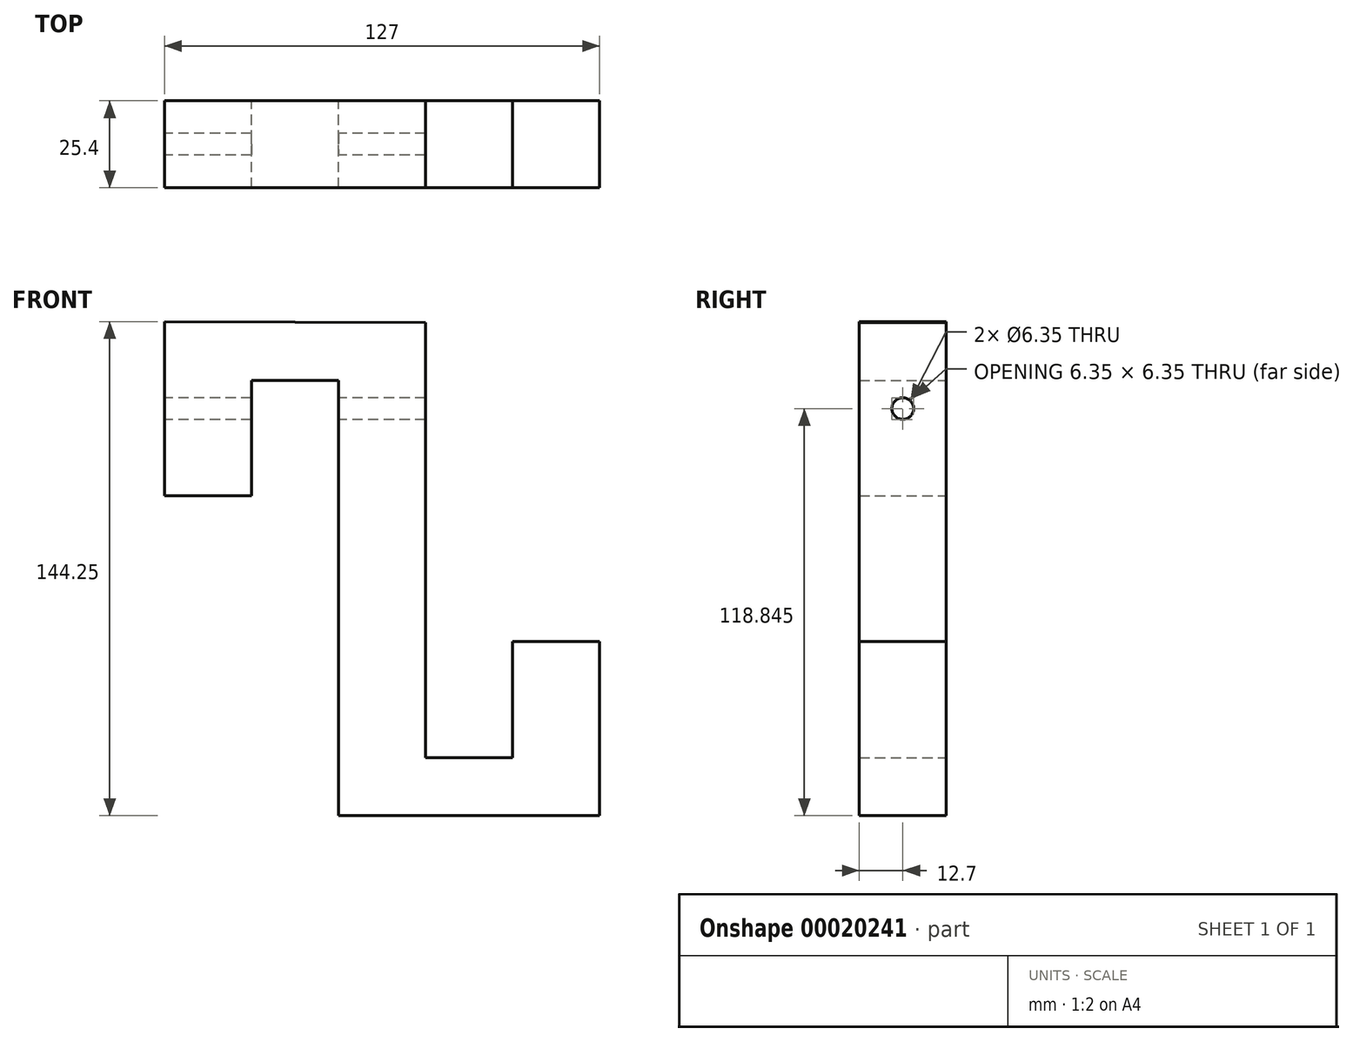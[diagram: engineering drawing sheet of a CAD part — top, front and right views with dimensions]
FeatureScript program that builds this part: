
annotation { "Feature Type Name" : "Feature", "Feature Type Description" : "" }
export const myFeature = defineFeature(function(context is Context, id is Id, definition is map)
    precondition{}
    {
        {
            var Q0;
            Q0=qCreatedBy(makeId("Front.planeOp"),FACE);
            var sketch = newSketch(context, id + "F0", { "sketchPlane" : qUnion([Q0])});
            skLineSegment(sketch, "E0", {"start": v(0, 71.41) * mm, "end": v(0, -55.59) * mm});
            skLineSegment(sketch, "E1", {"start": v(0, -55.59) * mm, "end": v(25.4, -55.59) * mm});
            skLineSegment(sketch, "E2", {"start": v(25.4, -55.59) * mm, "end": v(25.4, -21.7) * mm});
            skLineSegment(sketch, "E3", {"start": v(25.4, -21.7) * mm, "end": v(50.8, -21.7) * mm});
            skLineSegment(sketch, "E4", {"start": v(50.8, -21.7) * mm, "end": v(50.8, -72.5) * mm});
            skLineSegment(sketch, "E5", {"start": v(50.8, -72.5) * mm, "end": v(-25.4, -72.5) * mm});
            skLineSegment(sketch, "E6", {"start": v(-25.4, -72.5) * mm, "end": v(-25.4, 54.5) * mm});
            skLineSegment(sketch, "E7", {"start": v(-25.4, 54.5) * mm, "end": v(-50.8, 54.5) * mm});
            skLineSegment(sketch, "E8", {"start": v(-50.8, 54.5) * mm, "end": v(-50.8, 20.95) * mm});
            skLineSegment(sketch, "E9", {"start": v(-50.8, 20.95) * mm, "end": v(-76.2, 20.95) * mm});
            skLineSegment(sketch, "E10", {"start": v(-76.2, 20.95) * mm, "end": v(-76.2, 71.75) * mm});
            skLineSegment(sketch, "E11", {"start": v(-76.2, 71.75) * mm, "end": v(0, 71.41) * mm});
            skSolve(sketch);
        }
        {
            var Q0;
            Q0=makeQuery(id+"F0.imprint","IMPRINT",FACE,{"disambiguationData":[TD([[makeQuery(id+"F0.imprint","IMPRINT",EDGE,{"derivedFrom":sQuery(id+"F0.wireOp",EDGE,"E0")}),-1.0]])]});
            extrude(context, id + "F1", {"entities" : qUnion([Q0]), "depth" : 25.4 * mm});
        }
        {
            var Q0;
            Q0=makeQuery(id+"F1.opExtrude","SWEPT_FACE",FACE,{"disambiguationData":[OSD([sQuery(id+"F0.wireOp",EDGE,"E10")])]});
            var sketch = newSketch(context, id + "F2", { "sketchPlane" : qUnion([Q0])});
            skLineSegment(sketch, "E12", {"start": v(12.7, 71.75) * mm, "end": v(12.7, 20.95) * mm, "construction": true});
            skLineSegment(sketch, "E13", {"start": v(0, 46.35) * mm, "end": v(25.4, 46.35) * mm, "construction": true});
            skCircle(sketch, "E14", {"center": v(12.7, 46.35) * mm, "radius": 4.44 * mm});
            skSolve(sketch);
        }
        {
            var Q0;
            Q0=sQuery(id+"F2.wireOp",VERTEX,"E14.center");
            var Q1;
            Q1=makeQuery(id+"F1.opExtrude","SWEPT_BODY",BODY,{"disambiguationData":[OSD([sQuery(id+"F0.wireOp",EDGE,"E0"),sQuery(id+"F0.wireOp",EDGE,"E1"),sQuery(id+"F0.wireOp",EDGE,"E2"),sQuery(id+"F0.wireOp",EDGE,"E3"),sQuery(id+"F0.wireOp",EDGE,"E4"),sQuery(id+"F0.wireOp",EDGE,"E5"),sQuery(id+"F0.wireOp",EDGE,"E6"),sQuery(id+"F0.wireOp",EDGE,"E7"),sQuery(id+"F0.wireOp",EDGE,"E8"),sQuery(id+"F0.wireOp",EDGE,"E9"),sQuery(id+"F0.wireOp",EDGE,"E10"),sQuery(id+"F0.wireOp",EDGE,"E11")])]});
            hole(context, id + "F3", {"style" : HoleStyle.SIMPLE, "holeDiameter" : 6.35 * mm, "endStyle" : HoleEndStyle.THROUGH, "locations" : qUnion([Q0]), "scope" : qUnion([Q1])});
        }
    });
